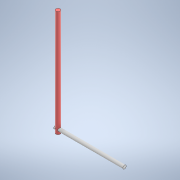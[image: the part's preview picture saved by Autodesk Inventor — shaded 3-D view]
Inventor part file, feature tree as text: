
AUTODESK INVENTOR PART (.ipt)
format: ipt  version: 2022.3 (Build 263350000, 350)  size: 102,400 bytes
history: native  units: in
note: dims shown in document units (in); Inventor stores cm internally (conversion verified against a paired STEP export)
features: extrude x2, sketch x2
ambient origin geometry x8: Origin, YZ Plane, XZ Plane, XY Plane, X Axis, Y Axis, Z Axis, Center Point
bodies: Solid1 (feature_tree)
feature tree (4):
  extrude  "Extrusion1"  Depth=5.0394in TaperAngle=0.0deg
  extrude  "Extrusion2"  Depth=3.1496in TaperAngle=0.0deg
  sketch  "Sketch1"  dims[d0=0.1969in d1=5.0394in d2=0.0in]
  sketch  "Sketch2"  dims[d3=0.1575in d4=3.1496in d5=0.0in d6=0.1181in d7=0.0in]
